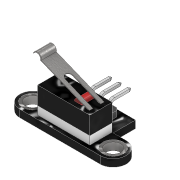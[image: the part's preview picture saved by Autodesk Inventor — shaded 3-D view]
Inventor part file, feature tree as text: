
AUTODESK INVENTOR PART (.ipt)
format: ipt  version: 2022 (Build 260153000, 153)  size: 425,984 bytes
history: native  units: mm
features: sketch x17, extrude x6, split x6, plane x4, loft x3, other x3, sweep x1
ambient origin geometry x8: Origin, YZ Plane, XZ Plane, XY Plane, X Axis, Y Axis, Z Axis, Center Point
bodies: Solid1 (feature_tree), Solid14 (feature_tree), Solid15 (feature_tree), Solid2 (feature_tree), Solid3 (feature_tree), Solid4 (feature_tree), Solid5 (feature_tree), Solid6 (feature_tree), Solid7 (feature_tree), Solid8 (feature_tree), Solid9 (feature_tree), Solid10 (feature_tree), Solid11 (feature_tree), Solid12 (feature_tree), Solid13 (feature_tree)
feature tree (40):
  extrude  "Extrusion1"  Depth=6.0mm
  extrude  "Extrusion2"  Depth=3.5mm
  plane  "Work Plane1"
  extrude  "Extrusion3"  Depth=4.0mm
  split  "Split1"
  split  "Split2"
  split  "Split3"
  split  "Split4"
  split  "Split5"
  plane  "Work Plane2"
  extrude  "Extrusion4"  Depth=3.0mm
  split  "Split6"
  extrude  "Extrusion5"  Depth=14.0mm
  extrude  "Extrusion6"  Depth=7.0mm TaperAngle=0.0deg
  sketch  "Sketch13"  dims[d25=-3.0mm]
  plane  "Work Plane3"
  sweep  "Sweep1"
  plane  "Work Plane4"
  loft  "Loft1"
  loft  "Loft2"
  loft  "Loft3"
  sketch  "Sketch1"  dims[d0=14.5mm d1=6.0mm]
  sketch  "Sketch2"  dims[d2=7.0mm d3=3.5mm]
  sketch  "Sketch3"  dims[d4=3.5mm d5=4.0mm]
  sketch  "Sketch4"  dims[d6=2.0mm d7=0.0mm d8=3.0mm]
  sketch  "Sketch5"  dims[d9=7.25mm d10=14.0mm]
  sketch  "Sketch6"  dims[d11=6.0mm d12=7.0mm d13=0.0mm]
  sketch  "Sketch7"  dims[d14=-1.0mm d15=27.576202mm]
  sketch  "Sketch8"  dims[d16=0.2mm d17=3.839724mm]
  sketch  "Sketch9"  dims[d18=0.2mm d19=1.0mm]
  sketch  "Sketch10"  dims[d20=4.0mm d21=0.0mm d22=5.5mm]
  sketch  "Sketch11"  dims[d23=5.5mm]
  sketch  "Sketch12"  dims[d24=5.5mm]
  sketch  "Sketch14"  dims[d26=1.0mm]
  sketch  "Sketch15"  dims[d27=3.5mm d28=0.0mm]
  other  "Edges1"
  sketch  "Sketch16"  dims[d29=1.0mm]
  other  "Edges2"
  sketch  "Sketch17"  dims[d30=2.0mm d31=2.0mm d32=0.0mm d33=1.5mm d34=0.0mm d35=0.32mm d36=3.5mm d37=5.0mm d38=1.0mm d39=0.0mm d40=0.0mm d41=0.5mm d42=0.2mm d43=0.2mm d44=0.2mm d45=0.2mm d46=0.24mm d47=0.24mm d48=0.24mm d49=0.24mm d50=0.24mm d51=0.24mm d52=0.0mm d53=90.0deg d54=0.0mm d55=90.0deg d56=0.2mm d57=0.2mm d58=0.24mm d59=0.24mm d60=0.0mm d61=90.0deg d62=0.0mm d63=90.0deg d64=0.2mm d65=0.2mm d66=0.24mm d67=0.24mm d68=0.0mm d69=90.0deg d70=0.0mm d71=90.0deg]
  other  "Edges3"
